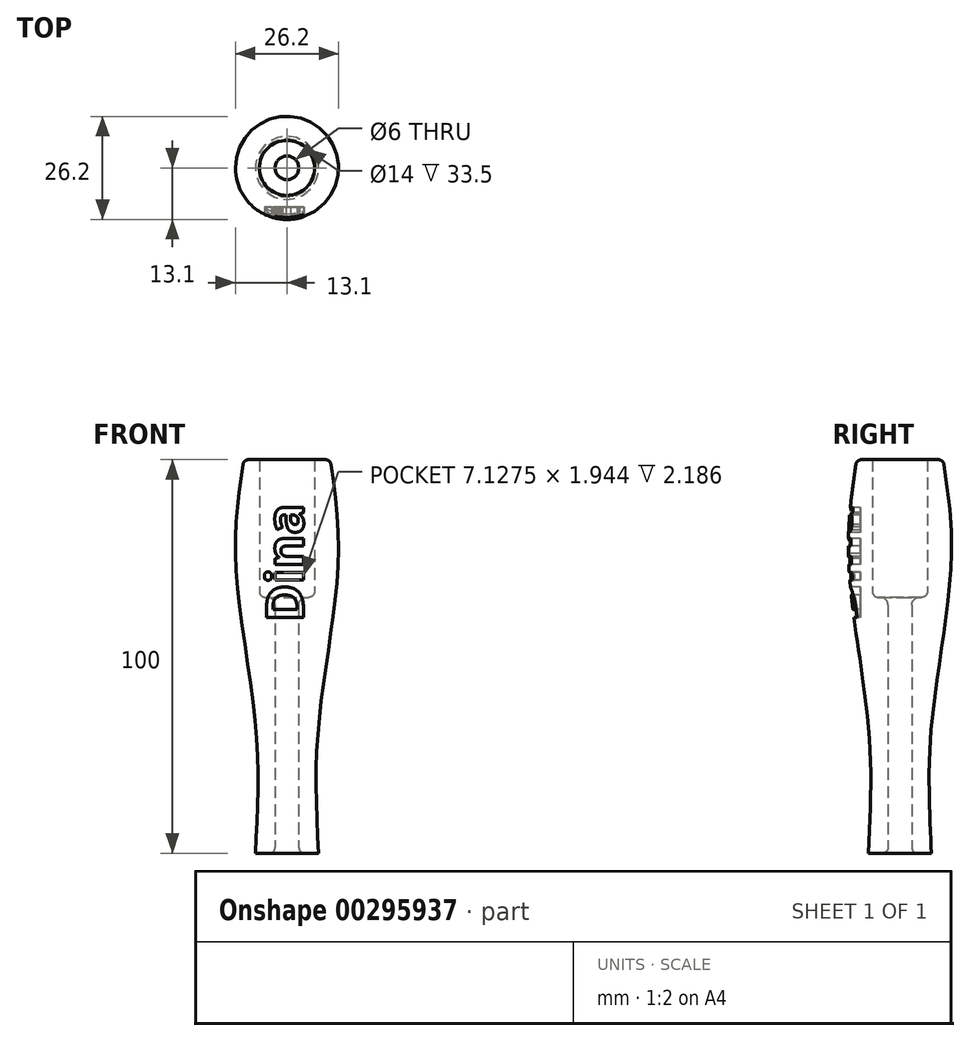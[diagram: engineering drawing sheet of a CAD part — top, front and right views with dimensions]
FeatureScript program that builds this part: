
annotation { "Feature Type Name" : "Feature", "Feature Type Description" : "" }
export const myFeature = defineFeature(function(context is Context, id is Id, definition is map)
    precondition{}
    {
        {
            var Q0;
            Q0=qCreatedBy(makeId("Front.planeOp"),FACE);
            var sketch = newSketch(context, id + "F0", { "sketchPlane" : qUnion([Q0])});
            skLineSegment(sketch, "E0", {"start": v(0, 0) * mm, "end": v(0, 100) * mm, "construction": true});
            skLineSegment(sketch, "E1", {"start": v(0, 100) * mm, "end": v(11, 100) * mm, "construction": true});
            skLineSegment(sketch, "E2", {"start": v(0, 0) * mm, "end": v(8, 0) * mm, "construction": true});
            skLineSegment(sketch, "E3.bottom", {"start": v(0, 0) * mm, "end": v(3, 0) * mm, "construction": true});
            skLineSegment(sketch, "E3.top", {"start": v(0, 4) * mm, "end": v(3, 4) * mm, "construction": true});
            skLineSegment(sketch, "E3.left", {"start": v(0, 0) * mm, "end": v(0, 4) * mm, "construction": true});
            skLineSegment(sketch, "E3.right", {"start": v(3, 0) * mm, "end": v(3, 4) * mm, "construction": true});
            skLineSegment(sketch, "E4.bottom", {"start": v(0, 100) * mm, "end": v(7, 100) * mm, "construction": true});
            skLineSegment(sketch, "E4.top", {"start": v(0, 65) * mm, "end": v(7, 65) * mm, "construction": true});
            skLineSegment(sketch, "E4.left", {"start": v(0, 100) * mm, "end": v(0, 65) * mm, "construction": true});
            skLineSegment(sketch, "E4.right", {"start": v(7, 100) * mm, "end": v(7, 65) * mm, "construction": true});
            skLineSegment(sketch, "E5", {"start": v(7, 100) * mm, "end": v(9.7, 100) * mm});
            skLineSegment(sketch, "E6", {"start": v(4.5, 0) * mm, "end": v(8, 0) * mm});
            skFitSpline(sketch, "E7", {"points": [v(8, 0) * mm, v(8, 32.1) * mm, v(13, 73.55) * mm, v(11, 100) * mm], "startDerivative": vector(-4.78, 93.1) * mm, "endDerivative": vector(-12.38, 82.63) * mm});
            skLineSegment(sketch, "E8", {"start": v(3, 1.5) * mm, "end": v(3, 63) * mm});
            skLineSegment(sketch, "E9", {"start": v(5, 65) * mm, "end": v(5.5, 65) * mm});
            skLineSegment(sketch, "E10", {"start": v(7, 100) * mm, "end": v(7, 66.5) * mm});
            skPoint(sketch, "E11.visualSharp", {"position": v(3, 65) * mm});
            skArc(sketch, "E11.filletArc", {"start": v(5, 65) * mm, "mid": v(3.59, 64.41) * mm, "end": v(3, 63) * mm});
            skPoint(sketch, "E12.visualSharp", {"position": v(7, 65) * mm});
            skArc(sketch, "E12.filletArc", {"start": v(5.5, 65) * mm, "mid": v(6.56, 65.44) * mm, "end": v(7, 66.5) * mm});
            skPoint(sketch, "E13.visualSharp", {"position": v(3, 0) * mm});
            skArc(sketch, "E13.filletArc", {"start": v(3, 1.5) * mm, "mid": v(3.44, 0.44) * mm, "end": v(4.5, 0) * mm});
            skArc(sketch, "E14.filletArc", {"start": v(11.2, 98.72) * mm, "mid": v(10.69, 99.64) * mm, "end": v(9.7, 100) * mm});
            skSolve(sketch);
        }
        {
            var Q0;
            Q0=makeQuery(id+"F0.imprint","IMPRINT",FACE,{"disambiguationData":[TD([[makeQuery(id+"F0.imprint","IMPRINT",EDGE,{"derivedFrom":sQuery(id+"F0.wireOp",EDGE,"E5")}),-1.0]])]});
            var Q1;
            Q1=sQuery(id+"F0.wireOp",EDGE,"E0");
            revolve(context, id + "F1", {"entities" : qUnion([Q0]), "axis" : qUnion([Q1]), "revolveType" : RevolveType.FULL});
        }
        {
            var Q0;
            Q0=qCreatedBy(makeId("Front.planeOp"),FACE);
            cPlane(context, id + "F2", {"entities" : qUnion([Q0]), "cplaneType" : CPlaneType.OFFSET, "offset" : 15 * mm, "width" : 150 * mm, "height" : 150 * mm});
        }
        {
            var Q0;
            Q0=qCreatedBy(id+"F2.planeOp",FACE);
            var sketch = newSketch(context, id + "F3", { "sketchPlane" : qUnion([Q0])});
            skLineSegment(sketch, "E15", {"start": v(4.16, 57.63) * mm, "end": v(4.16, 86.78) * mm, "construction": true});
            skText(sketch, "E16", { "text": "Dina", "fontName": "OpenSans-Bold.ttf"});
            const initialGuessF3  = {"E16": [0.00416, 0.05873, 0, 1, 0.0094]};
            skSetInitialGuess(sketch, initialGuessF3);
            skSolve(sketch);
        }
        {
            var Q0;
            Q0 = qSketchRegion(id + "F3", true);
            extrude(context, id + "F4", {"entities" : qUnion([Q0]), "operationType" : NewBodyOperationType.REMOVE, "oppositeDirection" : true, "depth" : 5 * mm});
        }
    });
